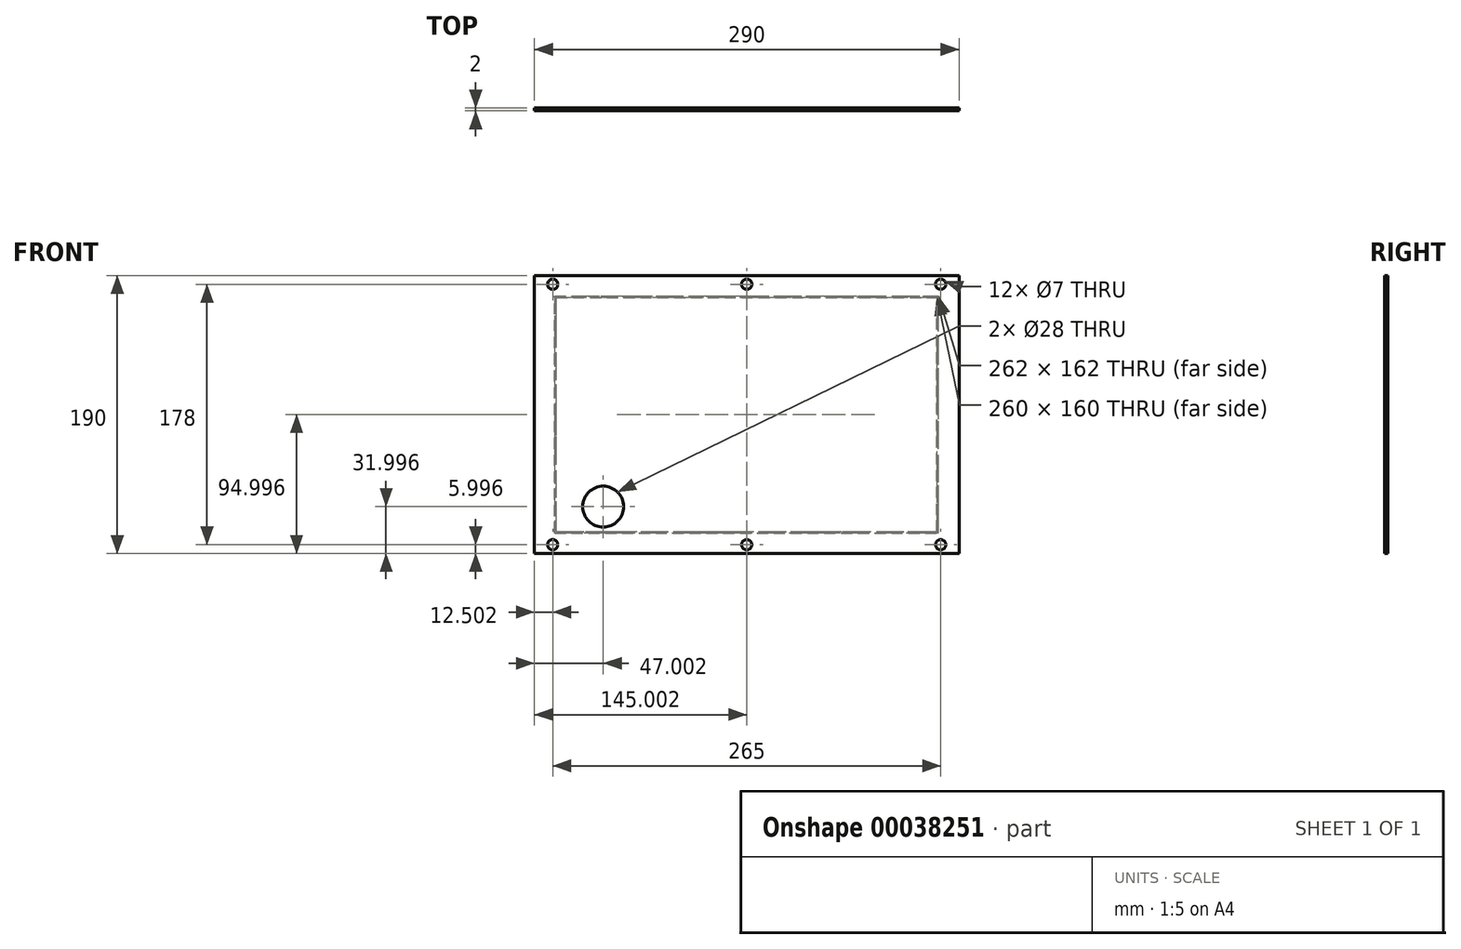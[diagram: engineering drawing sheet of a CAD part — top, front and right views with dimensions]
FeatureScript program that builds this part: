
annotation { "Feature Type Name" : "Feature", "Feature Type Description" : "" }
export const myFeature = defineFeature(function(context is Context, id is Id, definition is map)
    precondition{}
    {
        {
            var Q0;
            Q0=qCreatedBy(makeId("Front.planeOp"),FACE);
            var sketch = newSketch(context, id + "F0", { "sketchPlane" : qUnion([Q0])});
            skLineSegment(sketch, "E0.bottom", {"start": v(-108.62, -66.35) * mm, "end": v(181.38, -66.35) * mm});
            skLineSegment(sketch, "E0.top", {"start": v(-108.62, 123.65) * mm, "end": v(181.38, 123.65) * mm});
            skLineSegment(sketch, "E0.left", {"start": v(-108.62, -66.35) * mm, "end": v(-108.62, 123.65) * mm});
            skLineSegment(sketch, "E0.right", {"start": v(181.38, -66.35) * mm, "end": v(181.38, 123.65) * mm});
            skSolve(sketch);
        }
        {
            var Q0;
            Q0=makeQuery(id+"F0.imprint","IMPRINT",FACE,{"disambiguationData":[TD([[makeQuery(id+"F0.imprint","IMPRINT",EDGE,{"derivedFrom":sQuery(id+"F0.wireOp",EDGE,"E0.bottom")}),1.0]])]});
            extrude(context, id + "F1", {"entities" : qUnion([Q0]), "depth" : 2 * mm});
        }
        {
            var Q0;
            Q0=makeQuery(id+"F1.opExtrude","CAP_FACE",FACE,{"disambiguationData":[OSD([sQuery(id+"F0.wireOp",EDGE,"E0.bottom"),sQuery(id+"F0.wireOp",EDGE,"E0.top"),sQuery(id+"F0.wireOp",EDGE,"E0.left"),sQuery(id+"F0.wireOp",EDGE,"E0.right")])],"isStart":false});
            var sketch = newSketch(context, id + "F2", { "sketchPlane" : qUnion([Q0])});
            skLineSegment(sketch, "E1", {"start": v(-96.12, 136.11) * mm, "end": v(-96.12, -74.31) * mm});
            skLineSegment(sketch, "E2", {"start": v(36.38, 146.54) * mm, "end": v(36.38, -81.28) * mm});
            skLineSegment(sketch, "E3", {"start": v(168.88, 146.72) * mm, "end": v(168.88, -82.99) * mm});
            skLineSegment(sketch, "E4", {"start": v(-139.3, 117.65) * mm, "end": v(210.32, 117.65) * mm});
            skLineSegment(sketch, "E5", {"start": v(-145.42, -60.35) * mm, "end": v(213.2, -60.35) * mm});
            skPoint(sketch, "E6", {"position": v(-96.12, 117.65) * mm});
            skPoint(sketch, "E7", {"position": v(36.38, 117.65) * mm});
            skPoint(sketch, "E8", {"position": v(168.88, 117.65) * mm});
            skPoint(sketch, "E9", {"position": v(168.88, -60.35) * mm});
            skPoint(sketch, "E10", {"position": v(36.38, -60.35) * mm});
            skPoint(sketch, "E11", {"position": v(-96.12, -60.35) * mm});
            skSolve(sketch);
        }
        {
            var Q0;
            Q0=sQuery(id+"F2.wireOp",VERTEX,"E6");
            var Q1;
            Q1=sQuery(id+"F2.wireOp",VERTEX,"E7");
            var Q2;
            Q2=sQuery(id+"F2.wireOp",VERTEX,"E8");
            var Q3;
            Q3=sQuery(id+"F2.wireOp",VERTEX,"E9");
            var Q4;
            Q4=sQuery(id+"F2.wireOp",VERTEX,"E10");
            var Q5;
            Q5=sQuery(id+"F2.wireOp",VERTEX,"E11");
            var Q6;
            Q6=makeQuery(id+"F1.opExtrude","SWEPT_BODY",BODY,{"disambiguationData":[OSD([sQuery(id+"F0.wireOp",EDGE,"E0.bottom"),sQuery(id+"F0.wireOp",EDGE,"E0.top"),sQuery(id+"F0.wireOp",EDGE,"E0.left"),sQuery(id+"F0.wireOp",EDGE,"E0.right")])]});
            hole(context, id + "F3", {"style" : HoleStyle.SIMPLE, "holeDiameter" : 7 * mm, "endStyle" : HoleEndStyle.THROUGH, "locations" : qUnion([Q0, Q1, Q2, Q3, Q4, Q5]), "scope" : qUnion([Q6])});
        }
        {
            var Q0;
            Q0=makeQuery(id+"F0.imprint","IMPRINT",FACE,{"disambiguationData":[TD([[makeQuery(id+"F0.imprint","IMPRINT",EDGE,{"derivedFrom":sQuery(id+"F0.wireOp",EDGE,"E0.bottom")}),1.0]])]});
            var sketch = newSketch(context, id + "F4", { "sketchPlane" : qUnion([Q0])});
            skLineSegment(sketch, "E12.bottom", {"start": v(-93.62, -51.35) * mm, "end": v(166.38, -51.35) * mm});
            skLineSegment(sketch, "E12.top", {"start": v(-93.62, 108.65) * mm, "end": v(166.38, 108.65) * mm});
            skLineSegment(sketch, "E12.left", {"start": v(-93.62, -51.35) * mm, "end": v(-93.62, 108.65) * mm});
            skLineSegment(sketch, "E12.right", {"start": v(166.38, -51.35) * mm, "end": v(166.38, 108.65) * mm});
            skLineSegment(sketch, "E13.1", {"start": v(-94.62, -52.35) * mm, "end": v(-94.62, 109.65) * mm});
            skLineSegment(sketch, "E13.2", {"start": v(-94.62, -52.35) * mm, "end": v(167.38, -52.35) * mm});
            skLineSegment(sketch, "E13.3", {"start": v(167.38, -52.35) * mm, "end": v(167.38, 109.65) * mm});
            skLineSegment(sketch, "E14", {"start": v(-94.62, 109.65) * mm, "end": v(167.38, 109.65) * mm});
            skSolve(sketch);
        }
        {
            var Q0;
            Q0=makeQuery(id+"F4.imprint","IMPRINT",FACE,{"disambiguationData":[TD([[makeQuery(id+"F4.imprint","IMPRINT",EDGE,{"derivedFrom":sQuery(id+"F4.wireOp",EDGE,"E12.bottom")}),-1.0]])]});
            extrude(context, id + "F5", {"entities" : qUnion([Q0]), "operationType" : NewBodyOperationType.REMOVE, "depth" : .2 * mm});
        }
        {
            var Q0;
            Q0=makeQuery(id+"F1.opExtrude","CAP_FACE",FACE,{"disambiguationData":[OSD([sQuery(id+"F0.wireOp",EDGE,"E0.bottom"),sQuery(id+"F0.wireOp",EDGE,"E0.top"),sQuery(id+"F0.wireOp",EDGE,"E0.left"),sQuery(id+"F0.wireOp",EDGE,"E0.right")])],"isStart":false});
            var sketch = newSketch(context, id + "F6", { "sketchPlane" : qUnion([Q0])});
            skLineSegment(sketch, "E15", {"start": v(-85.11, -34.35) * mm, "end": v(-23.6, -34.35) * mm});
            skLineSegment(sketch, "E16", {"start": v(-61.62, -2.53) * mm, "end": v(-61.62, -42.58) * mm});
            skPoint(sketch, "E17", {"position": v(-61.62, -34.35) * mm});
            skSolve(sketch);
        }
        {
            var Q0;
            Q0=sQuery(id+"F6.wireOp",VERTEX,"E17");
            var Q1;
            Q1=makeQuery(id+"F1.opExtrude","SWEPT_BODY",BODY,{"disambiguationData":[OSD([sQuery(id+"F0.wireOp",EDGE,"E0.bottom"),sQuery(id+"F0.wireOp",EDGE,"E0.top"),sQuery(id+"F0.wireOp",EDGE,"E0.left"),sQuery(id+"F0.wireOp",EDGE,"E0.right")])]});
            hole(context, id + "F7", {"style" : HoleStyle.SIMPLE, "holeDiameter" : 28 * mm, "endStyle" : HoleEndStyle.THROUGH, "locations" : qUnion([Q0]), "scope" : qUnion([Q1])});
        }
    });
